# Revit family: Lighting-UrbanLighting-GEWISS-EXTRO-FLOODLIGHT-LED_MULTIFUNCTIONAL
name_source: partatom
category: Apparecchi per illuminazione
revit_build: Autodesk Revit 2016 (Build: 20161004_0715(x64)
units: mm (PartAtom-declared; Revit-internal decimal feet)

## family parameters
Basato su piano di lavoro = Sì
Condiviso = No
Numero OmniClass = 23.80.70.14.21
Punto di calcolo locali = No
Quota connettore circolare = Usa diametro
Sempre verticale = Sì
Sorgente d'illuminazione = Sì
Taglio con vuoti quando caricato = No
Tipo di parte = Normale
Titolo OmniClass = Street and Roadway Lighting

## types (5) — shared parameters
Altezza da terra = 915 mm
Angolo inclinazione = 0.00°
Application = Indoor / Outdoor
Carico apparente = 0 VA
Catalogue = LIGHTING
Catalogue Range = EXTRO
Colour temperature = 4000 K (Ra 80)
Cornice = GEWISS - Grigio Graffite
Efficiency class of integrated LEDs = A ÷ A++
Electrocod = 2424
Emetti da lunghezza linea = 610 mm
File diagramma fotometrico = GWS2406-S2401.IES
Filtro dei colori = 16777215
Glow Wire Test = 850°C
IDF = d8c22121-058f-4e74-a7fb-f7e70f37339f
IDT = b8042366-a842-4a78-9f94-425fb34d4234
IP degree = IP55
Immagine tipo = GWS2401.jpg
Insulation class = I
Larghezza = 260 mm  [stored 0.853018 ft]
Material = Technopolymer
Minimum distance from the illuminated object = 1m
Numero di poli = 1
Produttore = GEWISS S.p.A.
Prospetto di default = 1219 mm
Shock resistance = IK09
Staffaggio = GEWISS - Grigio Graffite
Struttura = GEWISS - Grigio Graffite
Technical sheet = https://www.gewiss.com
Type of lamp = LED
Type of light source = LED - Not replaceable
URL = https://www.gewiss.com
Variazione temperatura colore lampada con luminosità attenuata = <Nessuno>
Version file RFA = 18.0
Vetro led = GEWISS - Led - lm 1470 / Temp_4000 K (Ra 80)
Voltaggio = 0 V
Warranty = Can be extended for up to 5 years

## per-type parameters (varying)
| type | Colour | Descrizione | EAN code | Lumen output (lm) | Modello | System power | Version type | Voltage | Weight (kg) |
| GWS2406 - LED - 13W - With Sensore - Grey - IP55 | Graphite grey | EXTRO LED 13W 4000K 220-240V GR.PRES.S. | 8011564812239 | 790 | GWS2406 | 13W | LED with presence detector | 220 / 240 V - 50 / 60 Hz | 2,2 |
| GWS2402 - LED - 26W - Grey - IP55 | Graphite grey | EXTRO LED 26W 4000K 220-240V 50-60HZ GR. | 8011564812222 | 1470 | GWS2402 | 26W | LED | 220/240 V - 50/60 Hz - Stand alone | 3,4 |
| GWS2401B - LED - 13W - Blue - IP55 | Midnight blue | EXTRO LED 13W 3000K 220-240V 50-60HZ BL. | 8011564868786 | 790 | GWS2401B | 13W | LED | 220/240 V - 50/60 Hz - Stand alone | 2 |
| GWS2402B - LED - 26W - Blue - IP55 | Midnight blue | EXTRO LED 26W 3000K 220-240V 50-60HZ BL. | 8011564868793 | 1470 | GWS2402B | 26W | LED | 220/240 V - 50/60 Hz - Stand alone | 3,4 |
| GWS2401 - LED - 13W - Grey - IP55 | Graphite grey | EXTRO LED 13W 4000K 220-240V 50-60HZ GR. | 8011564812215 | 790 | GWS2401 | 13W | LED | 220/240 V - 50/60 Hz - Stand alone | 2 |

note: [stored X ft] marks values corroborated as IEEE doubles in the binary element streams (Revit-internal decimal feet)

## geometry (parser evidence)
native form markers: Blend x4
no freeform markers — native parametric forms only
